# Revit family: CHWB107_Chartham 500 medical basin noTH Rev00 - Copy
name_source: partatom
category: Generic Models
revit_build: Autodesk Revit 2015 (Build: 20140606_1530(x64)
units: mm (PartAtom-declared; Revit-internal decimal feet)

## types (1)
- SWC_WHB_CHWB107
    Basin mounting = Wall Mounted
    Brand = SanCeram
    Help = http://www.theswc.co.uk
    Manufacturer URL = www.theswc.co.uk
    NBS Reference Code = N13 - 335
    NBS Reference Description = WASH BASINS
    Name = Chartham 500 wall hung basin, back outlet, noTH
    Nominal Depth = 215 mm
    Nominal Length = 390 mm
    Nominal Width = 500 mm
    Overflow = No overflow
    Primary Finishes = Alpine White
    Primary Material = Vitreous China
    Product Family = Sanitary
    Product Group = Wall Hung Basin
    Product Information = http://www.theswc.co.uk
    Product SKU = CHWB107
    Spare Parts = http://www.theswc.co.uk
    Tap Holes = No tap holes
    Wash hand basin type = Clinical basin
    Waste type = Back outlet, waste adaptor & fixing kit - TSWC110 (supplied seperatly)
    Weight = 10 kg

## geometry (parser evidence)
native form markers: Blend x4, Sweep x2
no freeform markers — native parametric forms only
